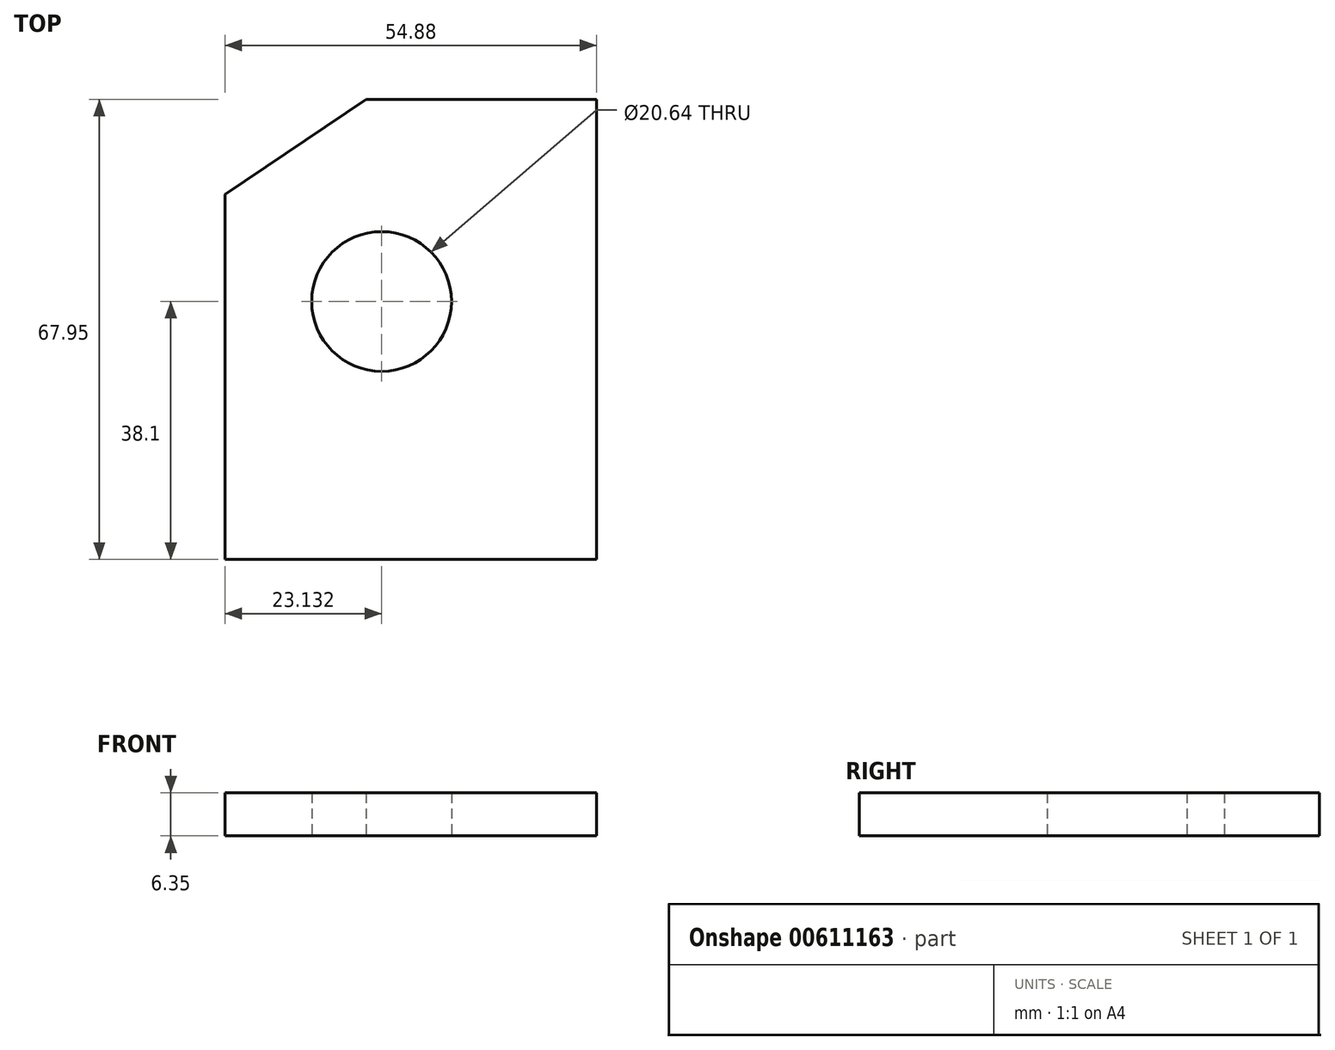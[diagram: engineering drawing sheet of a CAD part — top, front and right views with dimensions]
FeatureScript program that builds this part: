
annotation { "Feature Type Name" : "Feature", "Feature Type Description" : "" }
export const myFeature = defineFeature(function(context is Context, id is Id, definition is map)
    precondition{}
    {
        {
            var Q0;
            Q0=qCreatedBy(makeId("Top.planeOp"),FACE);
            var sketch = newSketch(context, id + "F0", { "sketchPlane" : qUnion([Q0])});
            skLineSegment(sketch, "E0", {"start": v(9.64, 67.95) * mm, "end": v(43.66, 67.95) * mm});
            skLineSegment(sketch, "E1", {"start": v(43.66, 67.95) * mm, "end": v(43.66, 0) * mm});
            skLineSegment(sketch, "E2", {"start": v(43.66, 0) * mm, "end": v(-11.22, 0) * mm});
            skLineSegment(sketch, "E3", {"start": v(-11.22, 0) * mm, "end": v(-11.22, 53.9) * mm});
            skLineSegment(sketch, "E4", {"start": v(-11.22, 53.9) * mm, "end": v(9.64, 67.95) * mm});
            skPoint(sketch, "E5", {"position": v(11.91, 38.1) * mm});
            skSolve(sketch);
        }
        {
            var Q0;
            Q0=makeQuery(id+"F0.imprint","IMPRINT",FACE,{"disambiguationData":[TD([[makeQuery(id+"F0.imprint","IMPRINT",EDGE,{"derivedFrom":sQuery(id+"F0.wireOp",EDGE,"E0")}),-1.0]])]});
            extrude(context, id + "F1", {"entities" : qUnion([Q0]), "depth" : 6.35 * mm, "offsetDistance" : 25.4 * mm});
        }
        {
            var Q0;
            Q0=sQuery(id+"F0.wireOp",VERTEX,"E5");
            var Q1;
            Q1=makeQuery(id+"F1.opExtrude","SWEPT_BODY",BODY,{"disambiguationData":[OSD([sQuery(id+"F0.wireOp",EDGE,"E0"),sQuery(id+"F0.wireOp",EDGE,"E1"),sQuery(id+"F0.wireOp",EDGE,"E2"),sQuery(id+"F0.wireOp",EDGE,"E3"),sQuery(id+"F0.wireOp",EDGE,"E4")])]});
            hole(context, id + "F2", {"style" : HoleStyle.SIMPLE, "endStyle" : HoleEndStyle.THROUGH, "oppositeDirection" : true, "holeDiameter" : 20.64 * mm, "majorDiameter" : 6.35 * mm, "isTappedThrough" : true, "tappedDepth" : 12.7 * mm, "tapClearance" : 3, "locations" : qUnion([Q0]), "scope" : qUnion([Q1])});
        }
    });
